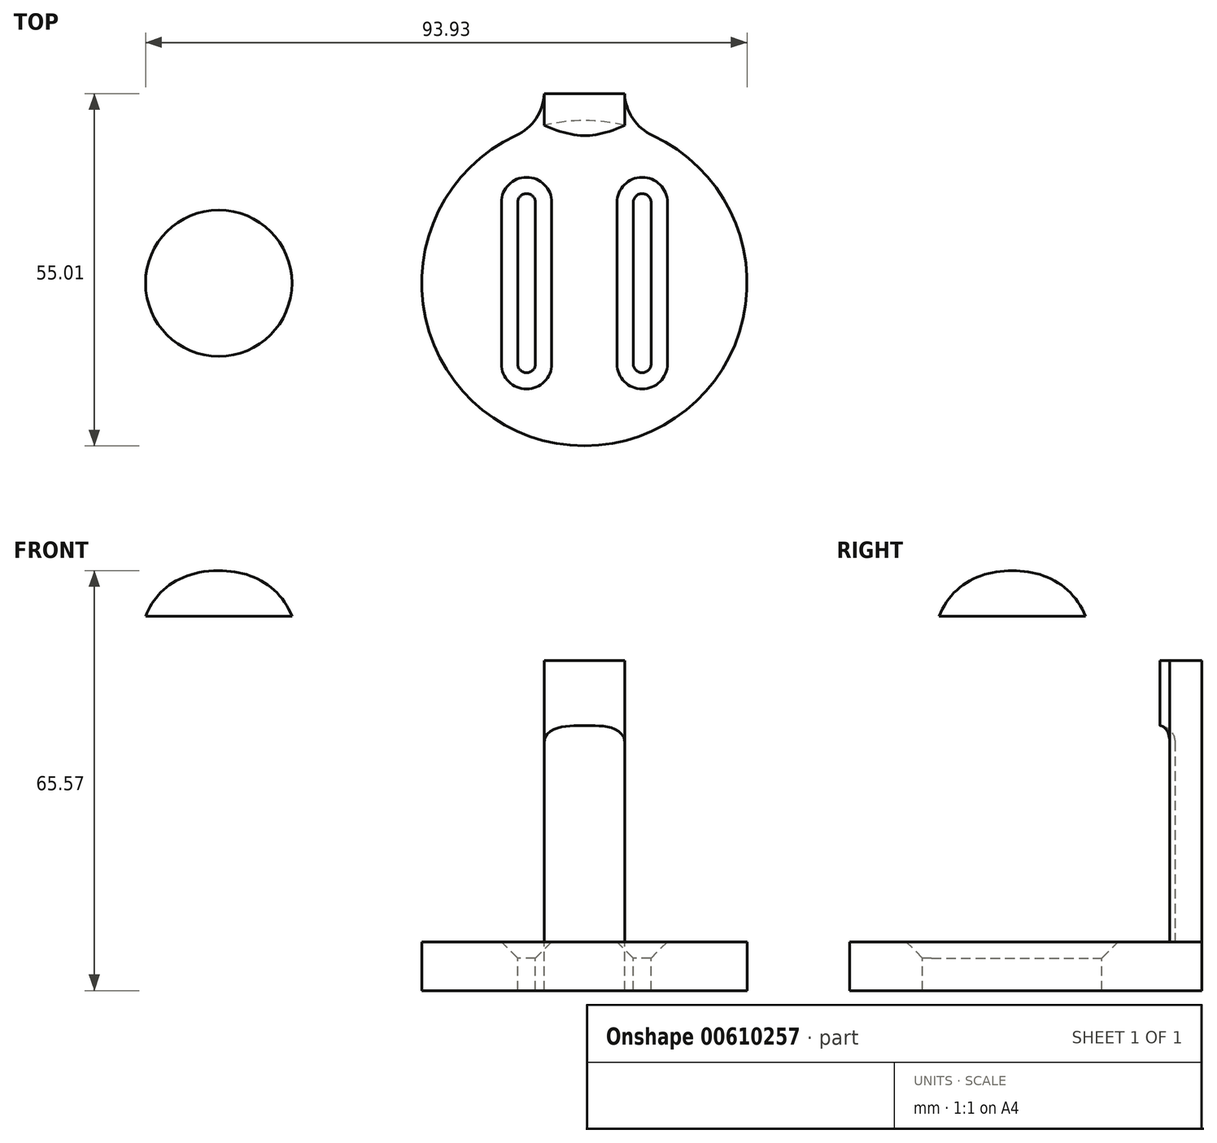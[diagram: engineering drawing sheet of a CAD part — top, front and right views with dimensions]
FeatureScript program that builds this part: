
annotation { "Feature Type Name" : "Feature", "Feature Type Description" : "" }
export const myFeature = defineFeature(function(context is Context, id is Id, definition is map)
    precondition{}
    {
        {
            var Q0;
            Q0=qCreatedBy(makeId("Top.planeOp"),FACE);
            var sketch = newSketch(context, id + "F0", { "sketchPlane" : qUnion([Q0])});
            skCircle(sketch, "E0", {"center": v(0, 0) * mm, "radius": 25.4 * mm});
            skLineSegment(sketch, "E1.bottom", {"start": v(-6.28, 29.61) * mm, "end": v(6.28, 29.61) * mm});
            skLineSegment(sketch, "E1.left", {"start": v(-6.28, 29.61) * mm, "end": v(-6.28, 24.61) * mm});
            skLineSegment(sketch, "E1.right", {"start": v(6.28, 29.61) * mm, "end": v(6.28, 24.61) * mm});
            skPoint(sketch, "E1.middle", {"position": v(0, 25.4) * mm});
            skPoint(sketch, "E1.top.start.orphan", {"position": v(-6.28, 21.19) * mm});
            skPoint(sketch, "E2.orphan", {"position": v(6.28, 21.19) * mm});
            skLineSegment(sketch, "E3.left", {"start": v(-10.42, 12.6) * mm, "end": v(-10.42, -12.6) * mm});
            skLineSegment(sketch, "E3.right", {"start": v(-7.64, 12.6) * mm, "end": v(-7.64, -12.6) * mm});
            skPoint(sketch, "E3.middle", {"position": v(-9.03, 0) * mm});
            skArc(sketch, "E4", {"start": v(-7.64, 12.6) * mm, "mid": v(-9.03, 13.99) * mm, "end": v(-10.42, 12.6) * mm});
            skArc(sketch, "E5", {"start": v(-10.42, -12.6) * mm, "mid": v(-9.03, -13.99) * mm, "end": v(-7.64, -12.6) * mm});
            skArc(sketch, "E6.MirrorCS", {"start": v(7.64, 12.6) * mm, "mid": v(9.03, 13.99) * mm, "end": v(10.42, 12.6) * mm});
            skLineSegment(sketch, "E7.MirrorCS", {"start": v(10.42, 12.6) * mm, "end": v(10.42, -12.6) * mm});
            skLineSegment(sketch, "E8.MirrorCS", {"start": v(7.64, 12.6) * mm, "end": v(7.64, -12.6) * mm});
            skArc(sketch, "E9.MirrorCS", {"start": v(10.42, -12.6) * mm, "mid": v(9.03, -13.99) * mm, "end": v(7.64, -12.6) * mm});
            skSolve(sketch);
        }
        {
            var Q0;
            Q0=makeQuery(id+"F0.imprint","IMPRINT",FACE,{"disambiguationData":[TD([[makeQuery(id+"F0.imprint","IMPRINT",EDGE,{"derivedFrom":sQuery(id+"F0.wireOp",EDGE,"E3.left")}),-1.0]])]});
            var Q1;
            Q1=makeQuery(id+"F0.imprint","IMPRINT",FACE,{"disambiguationData":[TD([[makeQuery(id+"F0.imprint","IMPRINT",EDGE,{"derivedFrom":sQuery(id+"F0.wireOp",EDGE,"E1.bottom")}),-1.0]])]});
            extrude(context, id + "F1", {"entities" : qUnion([Q0, Q1]), "oppositeDirection" : true, "depth" : 7.62 * mm, "offsetDistance" : 25.4 * mm});
        }
        {
            var Q0;
            Q0=makeQuery(id+"F1.opExtrude","CAP_EDGE",EDGE,{"disambiguationData":[OSD([sQuery(id+"F0.wireOp",EDGE,"E3.left")])],"isStart":true});
            var Q1;
            Q1=makeQuery(id+"F1.opExtrude","CAP_EDGE",EDGE,{"disambiguationData":[OSD([sQuery(id+"F0.wireOp",EDGE,"E8.MirrorCS")])],"isStart":true});
            chamfer(context, id + "F2", {"entities" : qUnion([Q0, Q1]), "width" : 2.54 * mm, "tangentPropagation" : true});
        }
        {
            var Q0;
            Q0=makeQuery(id+"F0.imprint","IMPRINT",FACE,{"disambiguationData":[TD([[makeQuery(id+"F0.imprint","IMPRINT",EDGE,{"derivedFrom":sQuery(id+"F0.wireOp",EDGE,"E1.bottom")}),-1.0]])]});
            extrude(context, id + "F3", {"entities" : qUnion([Q0]), "operationType" : NewBodyOperationType.ADD, "depth" : 43.94 * mm, "offsetDistance" : 25.4 * mm});
        }
        {
            var Q0;
            Q0=makeQuery(id+"F1.opExtrude","SWEPT_EDGE",EDGE,{"disambiguationData":[OSD([sQuery(id+"F0.wireOp",EDGE,"E0"),sQuery(id+"F0.wireOp",EDGE,"E1.left")])]});
            var Q1;
            Q1=makeQuery(id+"F1.opExtrude","SWEPT_EDGE",EDGE,{"disambiguationData":[OSD([sQuery(id+"F0.wireOp",EDGE,"E0"),sQuery(id+"F0.wireOp",EDGE,"E1.right")])]});
            fillet(context, id + "F4", {"entities" : qUnion([Q0, Q1]), "radius" : 7.62 * mm, "tangentPropagation" : true, "allowEdgeOverflow" : false});
        }
        {
            var Q0;
            Q0=makeQuery(id+"F3.opExtrude","CAP_FACE",FACE,{"disambiguationData":[OSD([sQuery(id+"F0.wireOp",EDGE,"E0"),sQuery(id+"F0.wireOp",EDGE,"E1.bottom"),sQuery(id+"F0.wireOp",EDGE,"E1.left"),sQuery(id+"F0.wireOp",EDGE,"E1.right")])],"isStart":false});
            var sketch = newSketch(context, id + "F5", { "sketchPlane" : qUnion([Q0])});
            skLineSegment(sketch, "E10", {"start": v(-6.28, 26.02) * mm, "end": v(6.28, 26.02) * mm});
            skLineSegment(sketch, "E11", {"start": v(6.28, 26.02) * mm, "end": v(6.28, 24.61) * mm});
            skLineSegment(sketch, "E12", {"start": v(6.28, 24.61) * mm, "end": v(-6.28, 24.61) * mm});
            skLineSegment(sketch, "E13", {"start": v(-6.28, 24.61) * mm, "end": v(-6.28, 26.02) * mm});
            skFitSpline(sketch, "E14", {"points": [v(-6.28, 24.61) * mm, v(6.28, 24.61) * mm], "startDerivative": vector(15.63, -6.28) * mm, "endDerivative": vector(14.9, 6.28) * mm});
            skSolve(sketch);
        }
        {
            var Q0;
            Q0=makeQuery(id+"F5.imprint","IMPRINT",FACE,{"disambiguationData":[TD([[makeQuery(id+"F5.imprint","IMPRINT",EDGE,{"derivedFrom":sQuery(id+"F5.wireOp",EDGE,"E12")}),1.0]])]});
            var Q1;
            Q1=makeQuery(id+"F5.imprint","IMPRINT",FACE,{"disambiguationData":[TD([[makeQuery(id+"F5.imprint","IMPRINT",EDGE,{"derivedFrom":sQuery(id+"F5.wireOp",EDGE,"E10")}),-1.0]])]});
            var Q2;
            Q2=makeQuery(id+"F5.imprint","IMPRINT",FACE,{"disambiguationData":[TD([[makeQuery(id+"F5.imprint","IMPRINT",EDGE,{"derivedFrom":sQuery(id+"F5.wireOp",EDGE,"E12")}),-1.0]])]});
            extrude(context, id + "F6", {"entities" : qUnion([Q0, Q1, Q2]), "operationType" : NewBodyOperationType.ADD, "oppositeDirection" : true, "depth" : 10.16 * mm, "offsetDistance" : 25.4 * mm});
        }
        {
            var Q0;
            Q0=makeQuery(id+"F6.boolean.opBoolean","INTERSECT",EDGE,{"derivedFrom":[makeQuery(id+"F3.opExtrude","SWEPT_FACE",FACE,{"disambiguationData":[OSD([sQuery(id+"F0.wireOp",EDGE,"E0")])]}),makeQuery(id+"F6.opExtrude","CAP_FACE",FACE,{"disambiguationData":[OSD([sQuery(id+"F5.wireOp",EDGE,"E10"),sQuery(id+"F5.wireOp",EDGE,"E11"),sQuery(id+"F5.wireOp",EDGE,"E13"),sQuery(id+"F5.wireOp",EDGE,"E14")])],"isStart":false})]});
            fillet(context, id + "F7", {"entities" : qUnion([Q0]), "radius" : 2.54 * mm, "tangentPropagation" : true, "allowEdgeOverflow" : false});
        }
        {
            var Q0;
            Q0=qCreatedBy(makeId("Front.planeOp"),FACE);
            var sketch = newSketch(context, id + "F8", { "sketchPlane" : qUnion([Q0])});
            skLineSegment(sketch, "E15", {"start": v(-57.1, 57.95) * mm, "end": v(-57.1, 50.84) * mm});
            skLineSegment(sketch, "E16", {"start": v(-57.1, 50.84) * mm, "end": v(-68.53, 50.84) * mm});
            skFitSpline(sketch, "E17", {"points": [v(-57.1, 57.95) * mm, v(-68.53, 50.84) * mm], "startDerivative": vector(-18.6, -0.04) * mm, "endDerivative": vector(-4.64, -11.81) * mm});
            skSolve(sketch);
        }
        {
            var Q0;
            Q0=makeQuery(id+"F8.imprint","IMPRINT",FACE,{"disambiguationData":[TD([[makeQuery(id+"F8.imprint","IMPRINT",EDGE,{"derivedFrom":sQuery(id+"F8.wireOp",EDGE,"E15")}),-1.0]])]});
            var Q1;
            Q1=sQuery(id+"F8.wireOp",EDGE,"E15");
            revolve(context, id + "F9", {"entities" : qUnion([Q0]), "axis" : qUnion([Q1]), "revolveType" : RevolveType.FULL});
        }
    });
